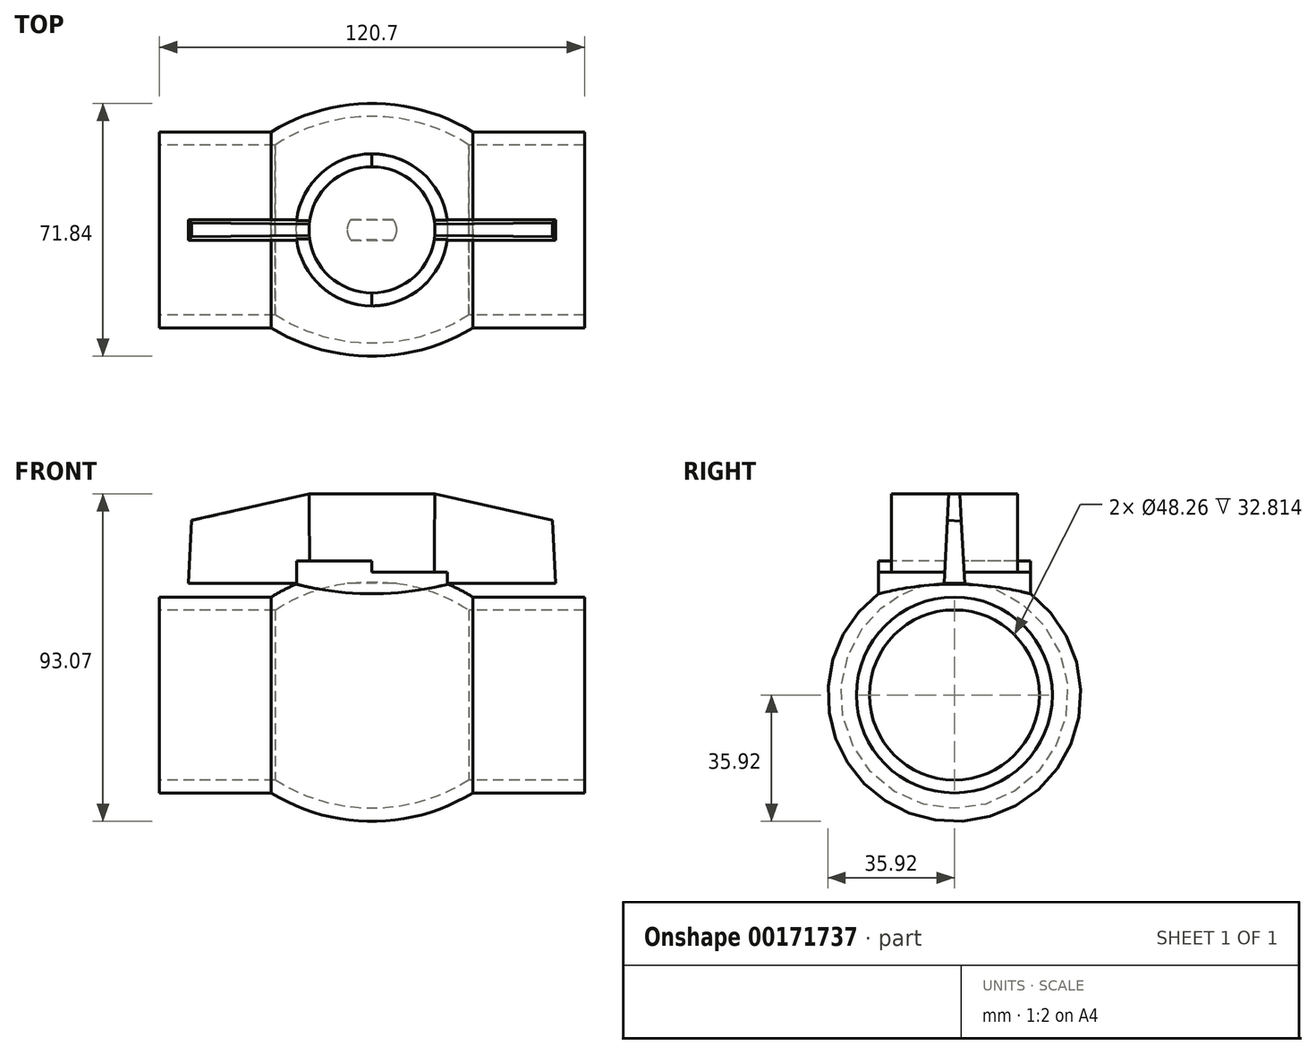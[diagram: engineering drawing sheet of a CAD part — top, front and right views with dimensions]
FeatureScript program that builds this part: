
annotation { "Feature Type Name" : "Feature", "Feature Type Description" : "" }
export const myFeature = defineFeature(function(context is Context, id is Id, definition is map)
    precondition{}
    {
        {
            var Q0;
            Q0=qCreatedBy(makeId("Top.planeOp"),FACE);
            var sketch = newSketch(context, id + "F0", { "sketchPlane" : qUnion([Q0])});
            skLineSegment(sketch, "E0", {"start": v(-34.95, 24.13) * mm, "end": v(-27.53, 24.13) * mm});
            skArc(sketch, "E1", {"start": v(27.53, 24.13) * mm, "mid": v(0, 32.24) * mm, "end": v(-27.53, 24.13) * mm});
            skLineSegment(sketch, "E2", {"start": v(27.53, 24.13) * mm, "end": v(34.95, 24.13) * mm});
            skLineSegment(sketch, "E3", {"start": v(34.95, 27.81) * mm, "end": v(34.95, 24.13) * mm});
            skLineSegment(sketch, "E4", {"start": v(34.95, 27.81) * mm, "end": v(28.6, 27.81) * mm});
            skArc(sketch, "E5", {"start": v(28.6, 27.81) * mm, "mid": v(0, 35.92) * mm, "end": v(-28.6, 27.81) * mm});
            skLineSegment(sketch, "E6", {"start": v(-28.6, 27.81) * mm, "end": v(-34.95, 27.81) * mm});
            skLineSegment(sketch, "E7", {"start": v(-34.95, 27.81) * mm, "end": v(-34.95, 24.13) * mm});
            skLineSegment(sketch, "E8", {"start": v(-30.9, 0) * mm, "end": v(45.75, 0) * mm});
            skSolve(sketch);
        }
        {
            var Q0;
            Q0 = qSketchRegion(id + "F0", true);
            var Q1;
            Q1=sQuery(id+"F0.wireOp",EDGE,"E8");
            revolve(context, id + "F1", {"entities" : qUnion([Q0]), "axis" : qUnion([Q1]), "revolveType" : RevolveType.FULL});
        }
        {
            var Q0;
            Q0=makeQuery(id+"F1.opRevolve","SWEPT_FACE",FACE,{"disambiguationData":[OSD([sQuery(id+"F0.wireOp",EDGE,"E3")])]});
            var sketch = newSketch(context, id + "F2", { "sketchPlane" : qUnion([Q0])});
            skCircle(sketch, "E9", {"center": v(0, 0) * mm, "radius": 24.13 * mm});
            skCircle(sketch, "E10", {"center": v(0, 0) * mm, "radius": 27.81 * mm});
            skSolve(sketch);
        }
        {
            var Q0;
            Q0 = qSketchRegion(id + "F2", true);
            extrude(context, id + "F3", {"entities" : qUnion([Q0]), "operationType" : NewBodyOperationType.ADD, "depth" : 25.4 * mm});
        }
        {
            var Q0;
            Q0=makeQuery(id+"F1.opRevolve","SWEPT_FACE",FACE,{"disambiguationData":[OSD([sQuery(id+"F0.wireOp",EDGE,"E7")])]});
            var sketch = newSketch(context, id + "F4", { "sketchPlane" : qUnion([Q0])});
            skCircle(sketch, "E11", {"center": v(0, 0) * mm, "radius": 24.13 * mm});
            skCircle(sketch, "E12", {"center": v(0, 0) * mm, "radius": 27.81 * mm});
            skSolve(sketch);
        }
        {
            var Q0;
            Q0 = qSketchRegion(id + "F4", true);
            extrude(context, id + "F5", {"entities" : qUnion([Q0]), "operationType" : NewBodyOperationType.ADD, "depth" : 25.4 * mm});
        }
        {
            var Q0;
            Q0=qCreatedBy(makeId("Top.planeOp"),FACE);
            cPlane(context, id + "F6", {"entities" : qUnion([Q0]), "cplaneType" : CPlaneType.OFFSET, "offset" : 38.1 * mm, "width" : 152.4 * mm, "height" : 152.4 * mm});
        }
        {
            var Q0;
            Q0=qCreatedBy(id+"F6.planeOp",FACE);
            var sketch = newSketch(context, id + "F7", { "sketchPlane" : qUnion([Q0])});
            skCircle(sketch, "E13", {"center": v(0, 0) * mm, "radius": 21.59 * mm});
            skCircle(sketch, "E14", {"center": v(0, 0) * mm, "radius": 17.9 * mm});
            skSolve(sketch);
        }
        {
            var Q0;
            Q0 = qSketchRegion(id + "F7", true);
            var Q1;
            Q1=makeQuery(id+"F1.opRevolve","SWEPT_FACE",FACE,{"disambiguationData":[OSD([sQuery(id+"F0.wireOp",EDGE,"E5")])]});
            extrude(context, id + "F8", {"entities" : qUnion([Q0]), "operationType" : NewBodyOperationType.ADD, "endBound" : BoundingType.UP_TO_SURFACE, "oppositeDirection" : true, "endBoundEntityFace" : qUnion([Q1]), "depth" : 25.4 * mm});
        }
        {
            var Q0;
            Q0=makeQuery(id+"F8.opExtrude","CAP_FACE",FACE,{"disambiguationData":[OSD([sQuery(id+"F7.wireOp",EDGE,"E13"),sQuery(id+"F7.wireOp",EDGE,"E14")])],"isStart":true});
            var sketch = newSketch(context, id + "F9", { "sketchPlane" : qUnion([Q0])});
            skCircle(sketch, "E15", {"center": v(0, 0) * mm, "radius": 17.9 * mm});
            skSolve(sketch);
        }
        {
            var Q0;
            Q0 = qSketchRegion(id + "F9", true);
            var Q1;
            Q1=makeQuery(id+"F1.opRevolve","SWEPT_FACE",FACE,{"disambiguationData":[OSD([sQuery(id+"F0.wireOp",EDGE,"E1")])]});
            extrude(context, id + "F10", {"entities" : qUnion([Q0]), "operationType" : NewBodyOperationType.REMOVE, "endBound" : BoundingType.UP_TO_SURFACE, "oppositeDirection" : true, "endBoundEntityFace" : qUnion([Q1]), "depth" : 25.4 * mm});
        }
        {
            var Q0;
            Q0=qCreatedBy(makeId("Right.planeOp"),FACE);
            cPlane(context, id + "F11", {"entities" : qUnion([Q0]), "cplaneType" : CPlaneType.OFFSET, "offset" : 21.59 * mm, "width" : 152.4 * mm, "height" : 152.4 * mm});
        }
        {
            var Q0;
            Q0=qCreatedBy(id+"F11.planeOp",FACE);
            var sketch = newSketch(context, id + "F12", { "sketchPlane" : qUnion([Q0])});
            skLineSegment(sketch, "E16.bottom", {"start": v(21.59, 38.1) * mm, "end": v(-21.6, 38.1) * mm});
            skLineSegment(sketch, "E16.top", {"start": v(21.59, 34.92) * mm, "end": v(-21.59, 34.92) * mm});
            skLineSegment(sketch, "E16.left", {"start": v(21.59, 38.1) * mm, "end": v(21.59, 34.92) * mm});
            skLineSegment(sketch, "E16.right", {"start": v(-21.6, 38.1) * mm, "end": v(-21.6, 34.92) * mm});
            skPoint(sketch, "E16.middle", {"position": v(0, 36.51) * mm});
            skSolve(sketch);
        }
        {
            var Q0;
            Q0 = qSketchRegion(id + "F12", true);
            var Q1;
            Q1=qCreatedBy(makeId("Right.planeOp"),FACE);
            extrude(context, id + "F13", {"entities" : qUnion([Q0]), "operationType" : NewBodyOperationType.REMOVE, "endBound" : BoundingType.UP_TO_SURFACE, "oppositeDirection" : true, "endBoundEntityFace" : qUnion([Q1]), "depth" : 21.59 * mm});
        }
        {
            var Q0;
            Q0=makeQuery(id+"F8.opExtrude","CAP_FACE",FACE,{"disambiguationData":[OSD([sQuery(id+"F7.wireOp",EDGE,"E13"),sQuery(id+"F7.wireOp",EDGE,"E14")])],"isStart":true});
            var sketch = newSketch(context, id + "F14", { "sketchPlane" : qUnion([Q0])});
            skCircle(sketch, "E17", {"center": v(0, 0) * mm, "radius": 17.9 * mm});
            skSolve(sketch);
        }
        {
            var Q0;
            Q0 = qSketchRegion(id + "F14", true);
            var Q1;
            Q1=makeQuery(id+"F1.opRevolve","SWEPT_FACE",FACE,{"disambiguationData":[OSD([sQuery(id+"F0.wireOp",EDGE,"E1")])]});
            extrude(context, id + "F15", {"entities" : qUnion([Q0]), "operationType" : NewBodyOperationType.ADD, "depth" : 19.05 * mm, "hasSecondDirection" : true, "secondDirectionBound" : SecondDirectionBoundingType.UP_TO_SURFACE, "secondDirectionOppositeDirection" : true, "secondDirectionBoundEntityFace" : qUnion([Q1]), "secondDirectionDepth" : 25.4 * mm});
        }
        {
            var Q0;
            Q0=makeQuery(id+"F15.opExtrude","CAP_FACE",FACE,{"disambiguationData":[OSD([sQuery(id+"F14.wireOp",EDGE,"E17")])],"isStart":false});
            var sketch = newSketch(context, id + "F16", { "sketchPlane" : qUnion([Q0])});
            skLineSegment(sketch, "E18", {"start": v(-50.8, 1.59) * mm, "end": v(-50.8, -1.59) * mm});
            skLineSegment(sketch, "E19", {"start": v(-50.8, -1.59) * mm, "end": v(50.8, -1.59) * mm});
            skLineSegment(sketch, "E20", {"start": v(50.8, -1.59) * mm, "end": v(50.8, 1.59) * mm});
            skLineSegment(sketch, "E21", {"start": v(50.8, 1.59) * mm, "end": v(-50.8, 1.59) * mm});
            skLineSegment(sketch, "E22", {"start": v(-50.8, 0) * mm, "end": v(50.8, 0) * mm});
            skSolve(sketch);
        }
        {
            var Q0;
            Q0 = qSketchRegion(id + "F16", true);
            extrude(context, id + "F17", {"entities" : qUnion([Q0]), "operationType" : NewBodyOperationType.ADD, "oppositeDirection" : true, "depth" : 25.4 * mm, "hasDraft" : true, "draftAngle" : 3 * degree});
        }
        {
            var Q0;
            {var subQ1=sQuery(id+"F16.wireOp",EDGE,"E18");var subQ5=sQuery(id+"F16.wireOp",EDGE,"E19");Q0=makeQuery(id+"F17.boolean.opBoolean","SPLIT",FACE,{"disambiguationData":[TD([makeQuery(id+"F17.opExtrude","SWEPT_FACE",FACE,{"disambiguationData":[OSD([subQ1])]})])],"derivedFrom":makeQuery(id+"F17.opExtrude","SWEPT_FACE",FACE,{"disambiguationData":[OSD([subQ5])]})});}
            var sketch = newSketch(context, id + "F18", { "sketchPlane" : qUnion([Q0])});
            skLineSegment(sketch, "E23", {"start": v(-17.84, 56.99) * mm, "end": v(-51.2, 49.37) * mm});
            skLineSegment(sketch, "E24", {"start": v(-51.2, 49.37) * mm, "end": v(-52.13, 31.55) * mm});
            skLineSegment(sketch, "E25", {"start": v(-52.13, 31.55) * mm, "end": v(-21.4, 31.55) * mm});
            skLineSegment(sketch, "E26", {"start": v(-21.4, 31.55) * mm, "end": v(-21.43, 37.91) * mm});
            skLineSegment(sketch, "E27", {"start": v(-21.43, 37.91) * mm, "end": v(-17.72, 37.91) * mm});
            skLineSegment(sketch, "E28", {"start": v(-17.72, 37.91) * mm, "end": v(-17.84, 56.99) * mm});
            skLineSegment(sketch, "E29", {"start": v(-17.84, 58.92) * mm, "end": v(-17.84, 56.99) * mm});
            skLineSegment(sketch, "E30", {"start": v(-17.84, 58.92) * mm, "end": v(-53.98, 58.92) * mm});
            skLineSegment(sketch, "E31", {"start": v(-53.98, 58.92) * mm, "end": v(-53.98, 49.37) * mm});
            skLineSegment(sketch, "E32", {"start": v(-53.98, 49.37) * mm, "end": v(-51.2, 49.37) * mm});
            skSolve(sketch);
        }
        {
            var Q0;
            Q0=makeQuery(id+"F18.imprint","IMPRINT",FACE,{"disambiguationData":[TD([[makeQuery(id+"F18.imprint","IMPRINT",EDGE,{"derivedFrom":sQuery(id+"F18.wireOp",EDGE,"E29")}),-1.0]])]});
            var Q1;
            {var subQ0=sQuery(id+"F18.wireOp",EDGE,"E23");Q1=makeQuery(id+"F18.imprint","IMPRINT",FACE,{"disambiguationData":[TD([[makeQuery(id+"F18.imprint","IMPRINT",EDGE,{"derivedFrom":subQ0}),-1.0]])]});}
            extrude(context, id + "F19", {"entities" : qUnion([Q0, Q1]), "operationType" : NewBodyOperationType.REMOVE, "endBound" : BoundingType.THROUGH_ALL, "oppositeDirection" : true, "depth" : 25.4 * mm});
        }
        {
            var Q0;
            {var subQ3=sQuery(id+"F16.wireOp",EDGE,"E19");Q0=makeQuery(id+"F17.boolean.opBoolean","SPLIT",FACE,{"disambiguationData":[TD([makeQuery(id+"F13.boolean.opBoolean","COPY",FACE,{"derivedFrom":makeQuery(id+"F13.opExtrude","SWEPT_FACE",FACE,{"disambiguationData":[OSD([sQuery(id+"F12.wireOp",EDGE,"E16.top")])]})})])],"derivedFrom":makeQuery(id+"F17.opExtrude","SWEPT_FACE",FACE,{"disambiguationData":[OSD([subQ3])]})});}
            var sketch = newSketch(context, id + "F20", { "sketchPlane" : qUnion([Q0])});
            skLineSegment(sketch, "E33", {"start": v(17.84, 56.99) * mm, "end": v(51.2, 49.37) * mm});
            skLineSegment(sketch, "E34", {"start": v(51.2, 49.37) * mm, "end": v(52.13, 31.55) * mm});
            skLineSegment(sketch, "E35", {"start": v(52.13, 31.55) * mm, "end": v(21.4, 31.55) * mm});
            skLineSegment(sketch, "E36", {"start": v(21.4, 31.55) * mm, "end": v(21.41, 34.73) * mm});
            skLineSegment(sketch, "E37", {"start": v(21.41, 34.73) * mm, "end": v(17.7, 34.73) * mm});
            skLineSegment(sketch, "E38", {"start": v(17.7, 34.73) * mm, "end": v(17.84, 56.99) * mm});
            skLineSegment(sketch, "E39", {"start": v(17.84, 56.99) * mm, "end": v(17.84, 61.65) * mm});
            skLineSegment(sketch, "E40", {"start": v(17.84, 61.65) * mm, "end": v(54.91, 61.65) * mm});
            skLineSegment(sketch, "E41", {"start": v(54.91, 61.65) * mm, "end": v(55.55, 49.37) * mm});
            skLineSegment(sketch, "E42", {"start": v(55.55, 49.37) * mm, "end": v(51.2, 49.37) * mm});
            skSolve(sketch);
        }
        {
            var Q0;
            Q0=makeQuery(id+"F20.imprint","IMPRINT",FACE,{"disambiguationData":[TD([[makeQuery(id+"F20.imprint","IMPRINT",EDGE,{"derivedFrom":sQuery(id+"F20.wireOp",EDGE,"E39")}),-1.0]])]});
            var Q1;
            {var subQ0=sQuery(id+"F20.wireOp",EDGE,"E33");Q1=makeQuery(id+"F20.imprint","IMPRINT",FACE,{"disambiguationData":[TD([[makeQuery(id+"F20.imprint","IMPRINT",EDGE,{"derivedFrom":subQ0}),1.0]])]});}
            extrude(context, id + "F21", {"entities" : qUnion([Q0, Q1]), "operationType" : NewBodyOperationType.REMOVE, "endBound" : BoundingType.THROUGH_ALL, "oppositeDirection" : true, "depth" : 25.4 * mm});
        }
    });
